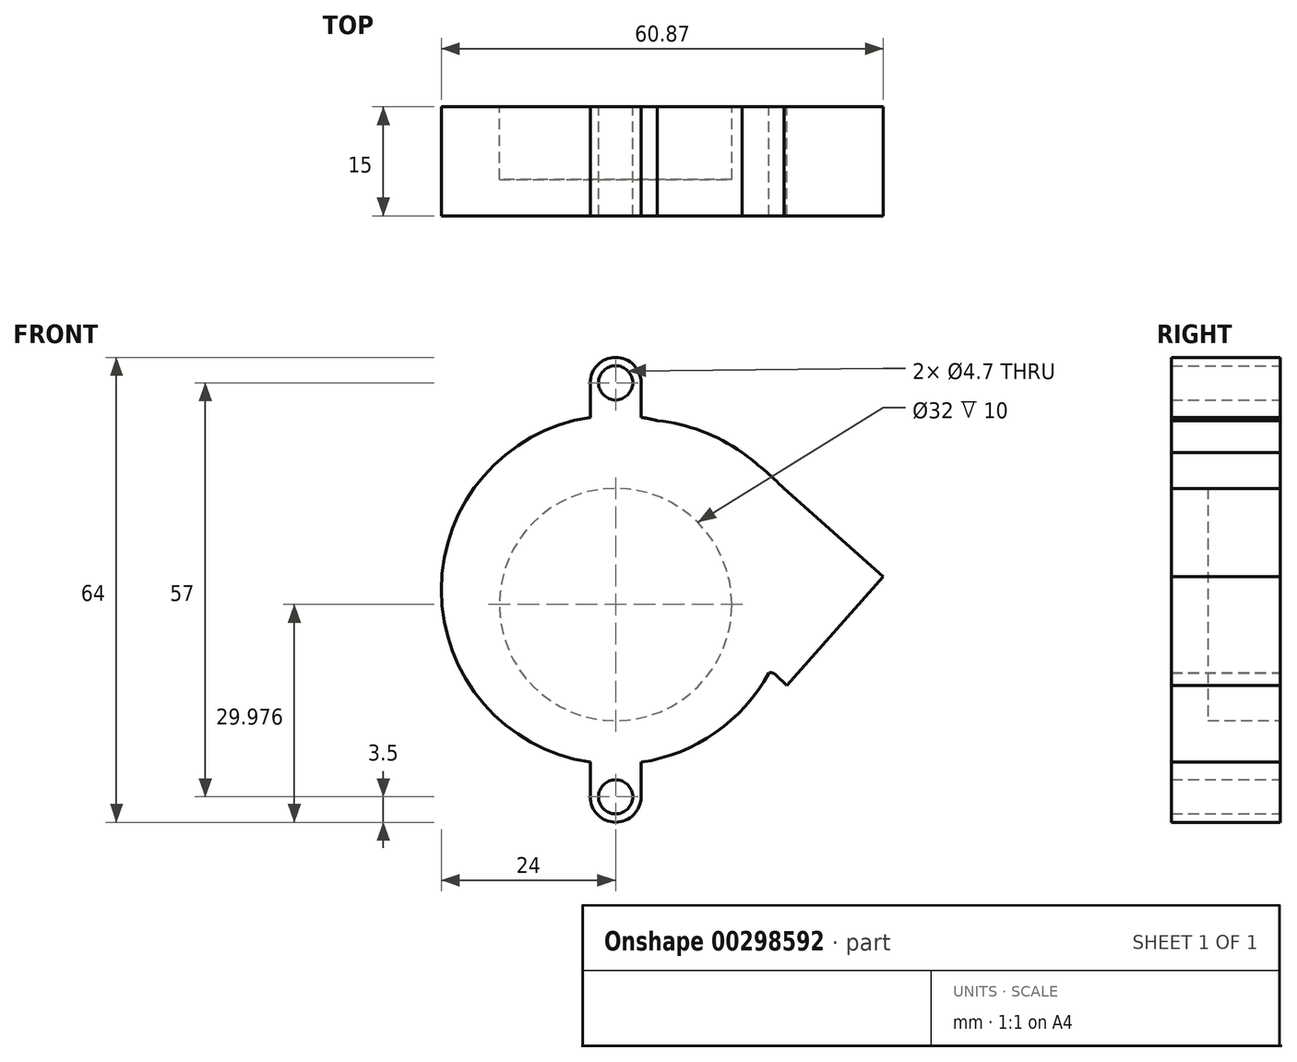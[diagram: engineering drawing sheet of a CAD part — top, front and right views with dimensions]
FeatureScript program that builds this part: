
annotation { "Feature Type Name" : "Feature", "Feature Type Description" : "" }
export const myFeature = defineFeature(function(context is Context, id is Id, definition is map)
    precondition{}
    {
        {
            var Q0;
            Q0=qCreatedBy(makeId("Front.planeOp"),FACE);
            var sketch = newSketch(context, id + "F0", { "sketchPlane" : qUnion([Q0])});
            skCircle(sketch, "E0", {"center": v(0, 0) * mm, "radius": 24 * mm});
            skPoint(sketch, "E1", {"position": v(0, 32) * mm});
            skPoint(sketch, "E2", {"position": v(0, -32) * mm});
            skLineSegment(sketch, "E3", {"start": v(-3.5, 35.65) * mm, "end": v(-3.5, -35.45) * mm, "construction": true});
            skLineSegment(sketch, "E4", {"start": v(3.5, 35.65) * mm, "end": v(3.5, -35.45) * mm, "construction": true});
            skCircle(sketch, "E5", {"center": v(0, 28.5) * mm, "radius": 3.5 * mm, "construction": true});
            skCircle(sketch, "E6", {"center": v(0, -28.5) * mm, "radius": 3.5 * mm, "construction": true});
            skArc(sketch, "E7", {"start": v(-3.5, 28.5) * mm, "mid": v(0, 32) * mm, "end": v(3.5, 28.5) * mm});
            skLineSegment(sketch, "E8", {"start": v(-3.5, 28.5) * mm, "end": v(-3.5, 23.74) * mm});
            skLineSegment(sketch, "E9", {"start": v(3.5, 28.5) * mm, "end": v(3.5, 23.74) * mm});
            skArc(sketch, "E10", {"start": v(-3.5, -28.5) * mm, "mid": v(0, -32) * mm, "end": v(3.5, -28.5) * mm});
            skLineSegment(sketch, "E11", {"start": v(-3.5, -28.5) * mm, "end": v(-3.5, -23.74) * mm});
            skLineSegment(sketch, "E12", {"start": v(3.5, -28.5) * mm, "end": v(3.5, -23.74) * mm});
            skCircle(sketch, "E13", {"center": v(0, 28.5) * mm, "radius": 2.35 * mm});
            skCircle(sketch, "E14", {"center": v(0, -28.5) * mm, "radius": 2.35 * mm});
            skLineSegment(sketch, "E15", {"start": v(23.6, -13.16) * mm, "end": v(36.87, 1.81) * mm});
            skLineSegment(sketch, "E16", {"start": v(23.6, -13.16) * mm, "end": v(22.02, -11.69) * mm});
            skLineSegment(sketch, "E17", {"start": v(36.87, 1.81) * mm, "end": v(23.2, 13.93) * mm});
            skArc(sketch, "E18", {"start": v(22.02, -11.69) * mm, "mid": v(21.6, -11.45) * mm, "end": v(21.1, -11.44) * mm});
            skArc(sketch, "E19", {"start": v(17.42, 18.9) * mm, "mid": v(11.86, 21.84) * mm, "end": v(5.76, 23.3) * mm});
            skArc(sketch, "E20", {"start": v(23.2, 13.93) * mm, "mid": v(20.4, 16.52) * mm, "end": v(17.42, 18.9) * mm});
            skSolve(sketch);
        }
        {
            var Q0;
            Q0=qSketchRegion(id+"F0",true);
            extrude(context, id + "F1", {"entities" : qUnion([Q0]), "depth" : 15 * mm});
        }
        {
            var Q0;
            Q0=makeQuery(id+"F1.opExtrude","CAP_FACE",FACE,{"disambiguationData":[OSD([sQuery(id+"F0.wireOp",EDGE,"E0"),sQuery(id+"F0.wireOp",EDGE,"E7"),sQuery(id+"F0.wireOp",EDGE,"E8"),sQuery(id+"F0.wireOp",EDGE,"E9"),sQuery(id+"F0.wireOp",EDGE,"E10"),sQuery(id+"F0.wireOp",EDGE,"E11"),sQuery(id+"F0.wireOp",EDGE,"E12"),sQuery(id+"F0.wireOp",EDGE,"E13"),sQuery(id+"F0.wireOp",EDGE,"E14"),sQuery(id+"F0.wireOp",EDGE,"E15"),sQuery(id+"F0.wireOp",EDGE,"E16"),sQuery(id+"F0.wireOp",EDGE,"E17"),sQuery(id+"F0.wireOp",EDGE,"E18"),sQuery(id+"F0.wireOp",EDGE,"E19"),sQuery(id+"F0.wireOp",EDGE,"E20")])],"isStart":true});
            var sketch = newSketch(context, id + "F2", { "sketchPlane" : qUnion([Q0])});
            skCircle(sketch, "E21", {"center": v(0, -2.02) * mm, "radius": 16 * mm});
            skSolve(sketch);
        }
        {
            var Q0;
            Q0=qSketchRegion(id+"F2",true);
            extrude(context, id + "F3", {"entities" : qUnion([Q0]), "operationType" : NewBodyOperationType.REMOVE, "oppositeDirection" : true, "depth" : 10 * mm});
        }
    });
